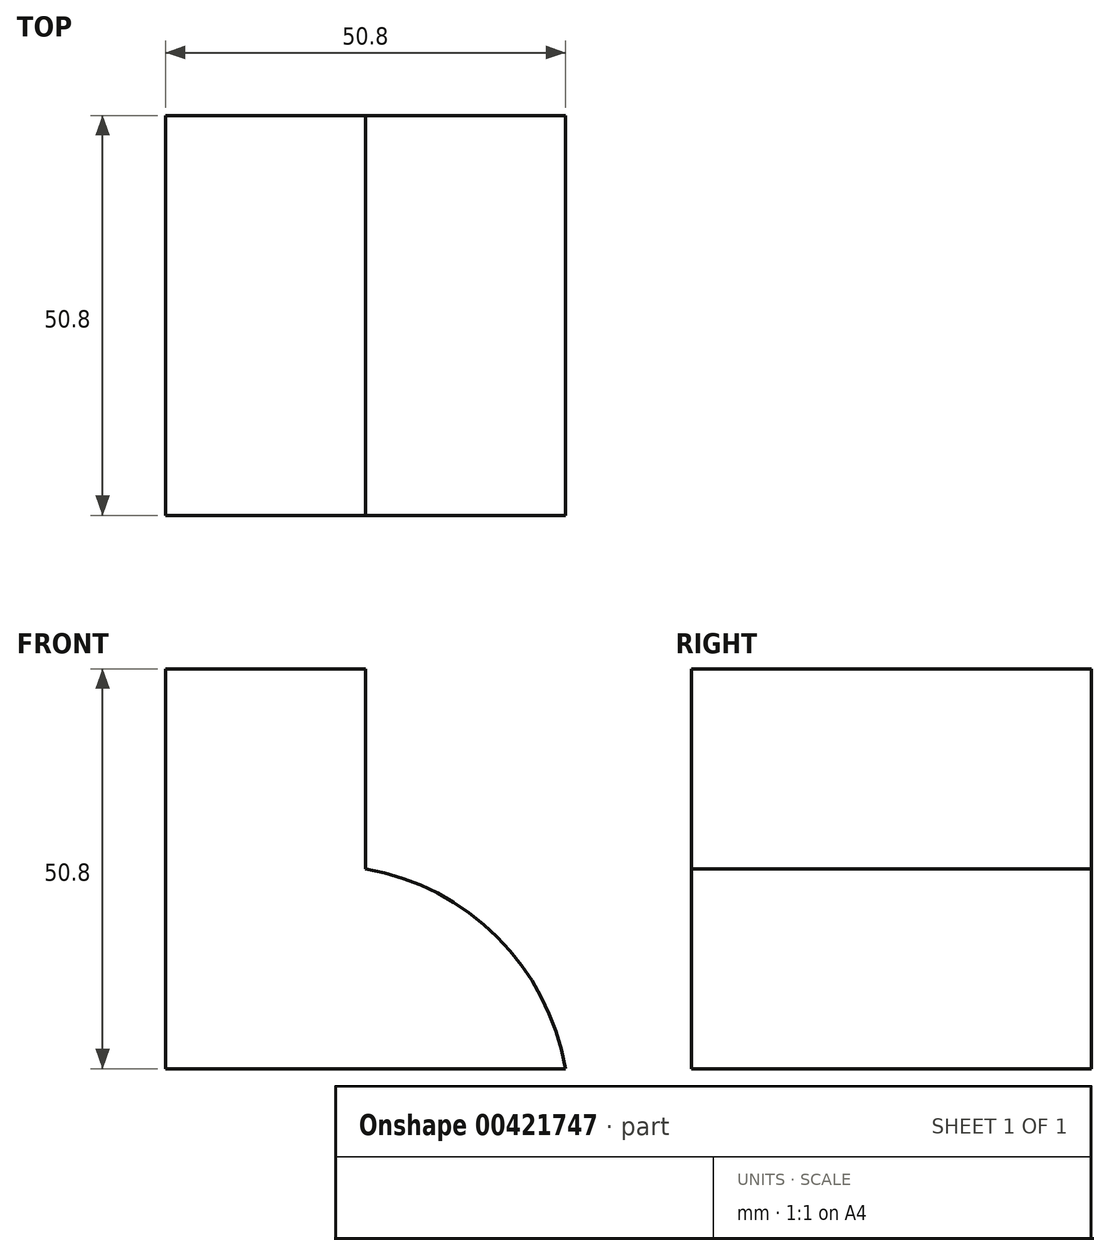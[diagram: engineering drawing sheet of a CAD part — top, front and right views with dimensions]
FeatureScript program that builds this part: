
annotation { "Feature Type Name" : "Feature", "Feature Type Description" : "" }
export const myFeature = defineFeature(function(context is Context, id is Id, definition is map)
    precondition{}
    {
        {
            var Q0;
            Q0=qCreatedBy(makeId("Front.planeOp"),FACE);
            var sketch = newSketch(context, id + "F0", { "sketchPlane" : qUnion([Q0])});
            skLineSegment(sketch, "E0", {"start": v(0, 0) * mm, "end": v(-50.8, 0) * mm});
            skLineSegment(sketch, "E1", {"start": v(-50.8, 0) * mm, "end": v(-50.8, 50.8) * mm});
            skLineSegment(sketch, "E2", {"start": v(-50.8, 50.8) * mm, "end": v(-25.4, 50.8) * mm});
            skLineSegment(sketch, "E3", {"start": v(-25.4, 50.8) * mm, "end": v(-25.4, 25.4) * mm});
            skArc(sketch, "E4", {"start": v(0, 0) * mm, "mid": v(-8.68, 16.72) * mm, "end": v(-25.4, 25.4) * mm});
            skSolve(sketch);
        }
        {
            var Q0;
            Q0=makeQuery(id+"F0.imprint","IMPRINT",FACE,{"disambiguationData":[TD([[makeQuery(id+"F0.imprint","IMPRINT",EDGE,{"derivedFrom":sQuery(id+"F0.wireOp",EDGE,"E0")}),-1.0]])]});
            extrude(context, id + "F1", {"entities" : qUnion([Q0]), "depth" : 50.8 * mm});
        }
    });
